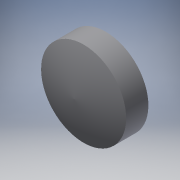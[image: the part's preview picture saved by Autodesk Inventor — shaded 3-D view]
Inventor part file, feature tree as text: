
AUTODESK INVENTOR PART (.ipt)
format: ipt  version: 2019.4 (Build 234330000, 330)  size: 119,296 bytes
history: native  units: mm
features: revolve x1, sketch x1
ambient origin geometry x8: Origin, YZ Plane, XZ Plane, XY Plane, X Axis, Y Axis, Z Axis, Center Point
bodies: Solid1 (feature_tree)
feature tree (2):
  revolve  "Revolution1"  [1 undecoded]
  sketch  "Sketch1"  dims[d0=9.0mm d1=4.7mm d2=2.0mm d3=90.0deg]
note: 1 required parameter value undecoded (feature->parameter linkage not recoverable at this tier; creation-order binding heuristic only, values carry confidence <= 0.55)
